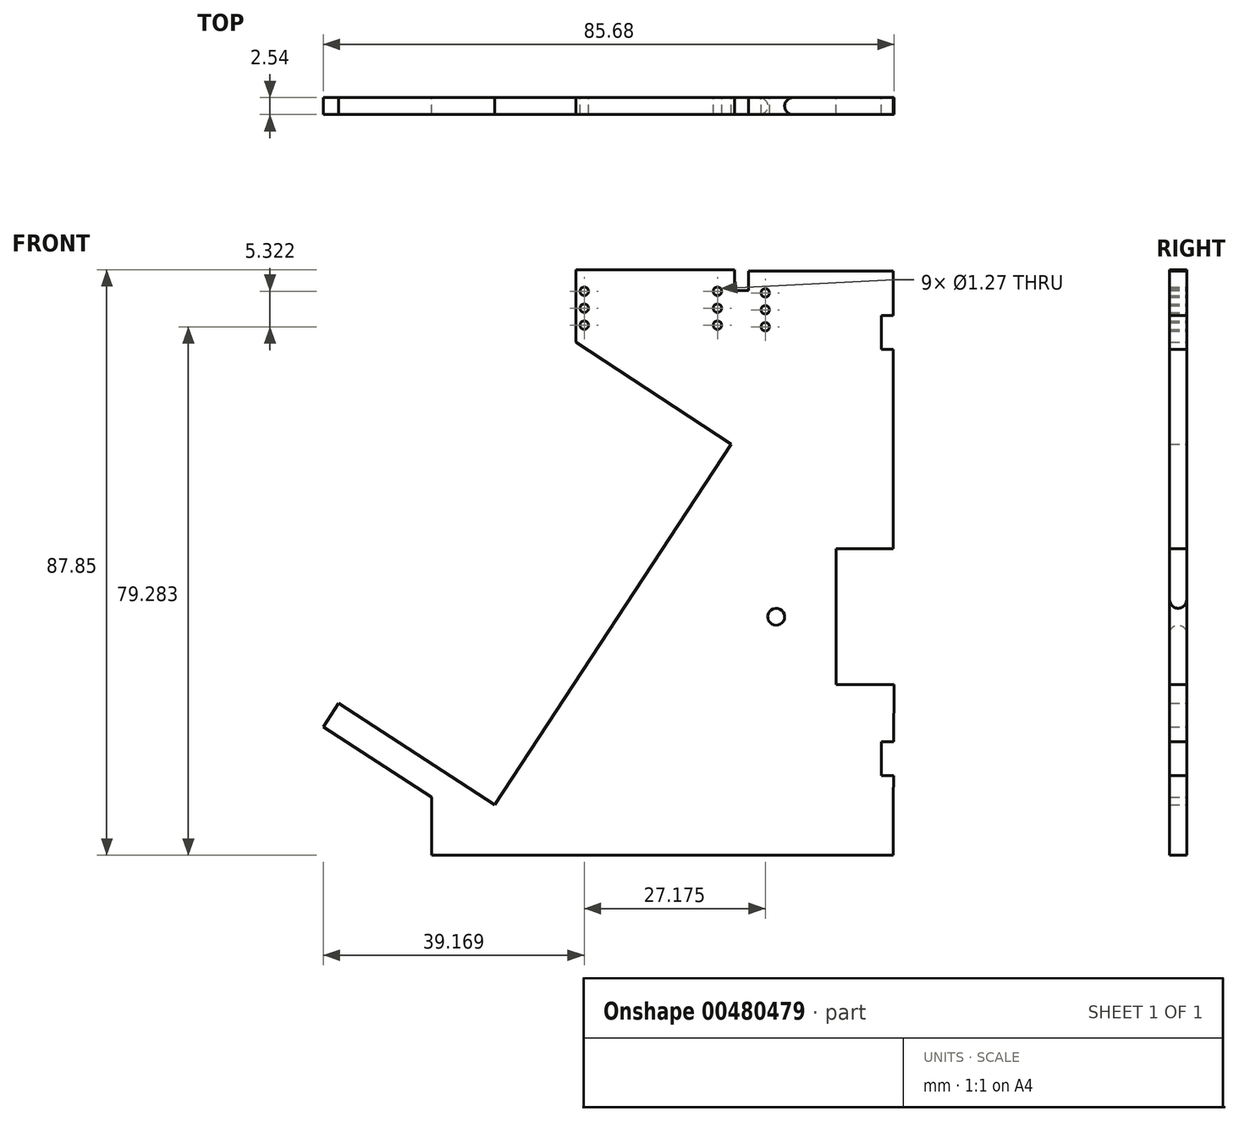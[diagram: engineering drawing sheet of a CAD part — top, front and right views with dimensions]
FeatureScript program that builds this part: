
annotation { "Feature Type Name" : "Feature", "Feature Type Description" : "" }
export const myFeature = defineFeature(function(context is Context, id is Id, definition is map)
    precondition{}
    {
        {
            var Q0;
            Q0=qCreatedBy(makeId("Front.planeOp"),FACE);
            var sketch = newSketch(context, id + "F0", { "sketchPlane" : qUnion([Q0])});
            skLineSegment(sketch, "E0.top", {"start": v(-8.7, 33.9) * mm, "end": v(15.1, 33.9) * mm});
            skLineSegment(sketch, "E0.right", {"start": v(15.1, 30.78) * mm, "end": v(15.1, 33.9) * mm});
            skLineSegment(sketch, "E1.top", {"start": v(15.1, 30.78) * mm, "end": v(17.2, 30.78) * mm});
            skLineSegment(sketch, "E1.right", {"start": v(38.95, 5.32) * mm, "end": v(38.95, 21.94) * mm});
            skPoint(sketch, "E2.orphan", {"position": v(38.95, -45.48) * mm});
            skLineSegment(sketch, "E3", {"start": v(39.35, 5) * mm, "end": v(39.24, -7.98) * mm});
            skLineSegment(sketch, "E4.top", {"start": v(39.24, -28.39) * mm, "end": v(39.08, -28.39) * mm});
            skLineSegment(sketch, "E5.trimOffspring", {"start": v(39.08, -28.39) * mm, "end": v(39.02, -36.93) * mm});
            skLineSegment(sketch, "E6.right", {"start": v(38.95, 30.78) * mm, "end": v(38.95, 27.02) * mm});
            skLineSegment(sketch, "E7.bottom", {"start": v(39.24, -7.98) * mm, "end": v(30.35, -7.98) * mm});
            skLineSegment(sketch, "E7.top", {"start": v(39.24, -28.39) * mm, "end": v(30.35, -28.39) * mm});
            skLineSegment(sketch, "E7.right", {"start": v(30.35, -7.98) * mm, "end": v(30.35, -28.39) * mm});
            skLineSegment(sketch, "E8.trimOffspring", {"start": v(38.95, -28.39) * mm, "end": v(38.95, -36.93) * mm});
            skPoint(sketch, "E9.orphan", {"position": v(-64, 19.6) * mm});
            skLineSegment(sketch, "E10.trimOffspring", {"start": v(-8.7, 23.02) * mm, "end": v(-8.7, 33.9) * mm});
            skLineSegment(sketch, "E11.trimOffspring", {"start": v(-8.7, 23.02) * mm, "end": v(-8.7, 30.64) * mm});
            skPoint(sketch, "E12.endSnap0", {"position": v(-8.7, 25.56) * mm});
            skLineSegment(sketch, "E13.trimOffspring", {"start": v(-8.7, 23.02) * mm, "end": v(-8.7, 28.59) * mm});
            skPoint(sketch, "E14.orphan", {"position": v(-8.7, 20.5) * mm});
            skLineSegment(sketch, "E15.top", {"start": v(17.2, 33.65) * mm, "end": v(38.95, 33.65) * mm});
            skLineSegment(sketch, "E15.left", {"start": v(17.2, 30.78) * mm, "end": v(17.2, 33.65) * mm});
            skLineSegment(sketch, "E15.right", {"start": v(38.95, 30.78) * mm, "end": v(38.95, 33.65) * mm});
            skPoint(sketch, "E16.end.orphan", {"position": v(-56.78, -28.13) * mm});
            skPoint(sketch, "E16.start.orphan", {"position": v(-54.5, -24.6) * mm});
            skPoint(sketch, "E17.start.orphan", {"position": v(-43.55, -36.67) * mm});
            skPoint(sketch, "E18.end.orphan", {"position": v(-41.27, -33.14) * mm});
            skPoint(sketch, "E18.start.orphan", {"position": v(-28.04, -41.7) * mm});
            skLineSegment(sketch, "E19", {"start": v(-44.32, -31.17) * mm, "end": v(-46.6, -34.7) * mm});
            skLineSegment(sketch, "E20", {"start": v(-20.88, -46.38) * mm, "end": v(14.65, 7.68) * mm});
            skLineSegment(sketch, "E21", {"start": v(-30.32, -45.22) * mm, "end": v(-30.32, -53.96) * mm});
            skLineSegment(sketch, "E22", {"start": v(38.95, -45.48) * mm, "end": v(38.95, -53.96) * mm});
            skLineSegment(sketch, "E23", {"start": v(38.95, -53.96) * mm, "end": v(-30.32, -53.96) * mm});
            skPoint(sketch, "E24.end.orphan", {"position": v(-10.8, 30.78) * mm});
            skPoint(sketch, "E24.start.orphan", {"position": v(-8.7, 30.78) * mm});
            skLineSegment(sketch, "E25.left", {"start": v(-8.7, 23.02) * mm, "end": v(-8.7, 38.26) * mm});
            skPoint(sketch, "E26.start.orphan", {"position": v(-9.4, 21.96) * mm});
            skLineSegment(sketch, "E27", {"start": v(-8.7, 23.02) * mm, "end": v(-8.7, 23.02) * mm});
            skPoint(sketch, "E28.end.orphan", {"position": v(-9.05, 23.02) * mm});
            skPoint(sketch, "E29.orphan", {"position": v(-9.4, 23.02) * mm});
            skLineSegment(sketch, "E30", {"start": v(14.65, 7.68) * mm, "end": v(-8.7, 23.02) * mm});
            skLineSegment(sketch, "E31", {"start": v(-20.88, -46.38) * mm, "end": v(-44.33, -31.19) * mm});
            skLineSegment(sketch, "E32", {"start": v(-46.6, -34.7) * mm, "end": v(-30.32, -45.22) * mm});
            skLineSegment(sketch, "E33.bottom", {"start": v(38.95, 27.02) * mm, "end": v(37.17, 27.02) * mm});
            skLineSegment(sketch, "E33.top", {"start": v(38.95, 21.94) * mm, "end": v(37.17, 21.94) * mm});
            skLineSegment(sketch, "E33.right", {"start": v(37.17, 27.02) * mm, "end": v(37.17, 21.94) * mm});
            skLineSegment(sketch, "E34.trimOffspring", {"start": v(38.95, 21.94) * mm, "end": v(38.95, -7.98) * mm});
            skLineSegment(sketch, "E35.trimOffspring", {"start": v(38.95, 27.02) * mm, "end": v(38.95, 30.78) * mm});
            skLineSegment(sketch, "E36.bottom", {"start": v(39.02, -36.93) * mm, "end": v(37.17, -36.93) * mm});
            skLineSegment(sketch, "E36.top", {"start": v(39.02, -42.01) * mm, "end": v(37.17, -42.01) * mm});
            skLineSegment(sketch, "E36.right", {"start": v(37.17, -36.93) * mm, "end": v(37.17, -42.01) * mm});
            skLineSegment(sketch, "E37.trimOffspring", {"start": v(38.95, -42.01) * mm, "end": v(38.95, -45.48) * mm});
            skLineSegment(sketch, "E38.trimOffspring", {"start": v(38.98, -42.01) * mm, "end": v(38.95, -45.48) * mm});
            skLineSegment(sketch, "E39", {"start": v(-7.43, 24.93) * mm, "end": v(-7.43, 26.2) * mm});
            skLineSegment(sketch, "E40", {"start": v(-8.07, 25.56) * mm, "end": v(-6.8, 25.56) * mm});
            skLineSegment(sketch, "E41", {"start": v(-6.8, 28.1) * mm, "end": v(-8.07, 28.1) * mm});
            skLineSegment(sketch, "E42", {"start": v(-8.7, 28.1) * mm, "end": v(-8.7, 30.64) * mm});
            skLineSegment(sketch, "E43", {"start": v(-8.07, 30.64) * mm, "end": v(-6.8, 30.64) * mm});
            skCircle(sketch, "E44", {"center": v(-7.43, 30.64) * mm, "radius": 0.64 * mm});
            skCircle(sketch, "E45", {"center": v(-7.43, 28.1) * mm, "radius": 0.64 * mm});
            skCircle(sketch, "E46", {"center": v(-7.43, 25.56) * mm, "radius": 0.64 * mm});
            skPoint(sketch, "E47.orphan", {"position": v(-7.43, 23.02) * mm});
            skPoint(sketch, "E48.orphan", {"position": v(-6.16, 23.02) * mm});
            skLineSegment(sketch, "E49.trimOffspring", {"start": v(-7.43, 27.47) * mm, "end": v(-7.43, 28.74) * mm});
            skPoint(sketch, "E50.orphan", {"position": v(-6.16, 28.1) * mm});
            skLineSegment(sketch, "E51.trimOffspring", {"start": v(-7.43, 30) * mm, "end": v(-7.43, 31.28) * mm});
            skPoint(sketch, "E52.orphan", {"position": v(-6.16, 25.56) * mm});
            skPoint(sketch, "E53.orphan", {"position": v(-6.16, 30.64) * mm});
            skLineSegment(sketch, "E54", {"start": v(-8.7, 23.02) * mm, "end": v(37.17, 23.02) * mm});
            skLineSegment(sketch, "E55", {"start": v(12.56, 24.93) * mm, "end": v(12.56, 26.2) * mm});
            skLineSegment(sketch, "E56", {"start": v(12.56, 25.56) * mm, "end": v(13.2, 25.56) * mm});
            skLineSegment(sketch, "E57", {"start": v(12.56, 28.1) * mm, "end": v(13.2, 28.1) * mm});
            skLineSegment(sketch, "E58", {"start": v(12.56, 30.64) * mm, "end": v(13.2, 30.64) * mm});
            skCircle(sketch, "E59", {"center": v(12.56, 30.64) * mm, "radius": 0.64 * mm});
            skCircle(sketch, "E60", {"center": v(12.56, 25.56) * mm, "radius": 0.64 * mm});
            skCircle(sketch, "E61", {"center": v(12.56, 28.1) * mm, "radius": 0.64 * mm});
            skLineSegment(sketch, "E62.trimOffspring", {"start": v(12.56, 27.47) * mm, "end": v(12.56, 31.28) * mm});
            skCircle(sketch, "E63.MirrorC", {"center": v(19.74, 30.4) * mm, "radius": 0.64 * mm});
            skCircle(sketch, "E64.MirrorC", {"center": v(19.74, 27.86) * mm, "radius": 0.64 * mm});
            skCircle(sketch, "E65.MirrorC", {"center": v(19.74, 25.32) * mm, "radius": 0.64 * mm});
            skPoint(sketch, "E66.start.orphan", {"position": v(16.15, 30.78) * mm});
            skLineSegment(sketch, "E67", {"start": v(15.1, 33.9) * mm, "end": v(33.91, 33.9) * mm});
            skLineSegment(sketch, "E68", {"start": v(4.31, -53.96) * mm, "end": v(4.31, -8.05) * mm});
            skLineSegment(sketch, "E69", {"start": v(4.31, -8.05) * mm, "end": v(4.31, -53.96) * mm});
            skLineSegment(sketch, "E70", {"start": v(21.38, -53.96) * mm, "end": v(21.38, 23.02) * mm});
            skLineSegment(sketch, "E71", {"start": v(30.35, -18.18) * mm, "end": v(21.38, -18.18) * mm});
            skCircle(sketch, "E72", {"center": v(21.38, -18.18) * mm, "radius": 1.27 * mm});
            skSolve(sketch);
        }
        {
            var Q0;
            Q0 = qSketchRegion(id + "F0", true);
            extrude(context, id + "F1", {"entities" : qUnion([Q0]), "depth" : 2.54 * mm});
        }
        {
            var Q0;
            Q0=makeQuery(id+"F1.opExtrude","CAP_EDGE",EDGE,{"disambiguationData":[OSD([sQuery(id+"F0.wireOp",EDGE,"E72")])],"isStart":false});
            var Q1;
            Q1=makeQuery(id+"F1.opExtrude","CAP_EDGE",EDGE,{"disambiguationData":[OSD([sQuery(id+"F0.wireOp",EDGE,"E72")])],"isStart":true});
            fillet(context, id + "F2", {"entities" : qUnion([Q0, Q1]), "radius" : 1.27 * mm, "tangentPropagation" : true, "allowEdgeOverflow" : false});
        }
    });
